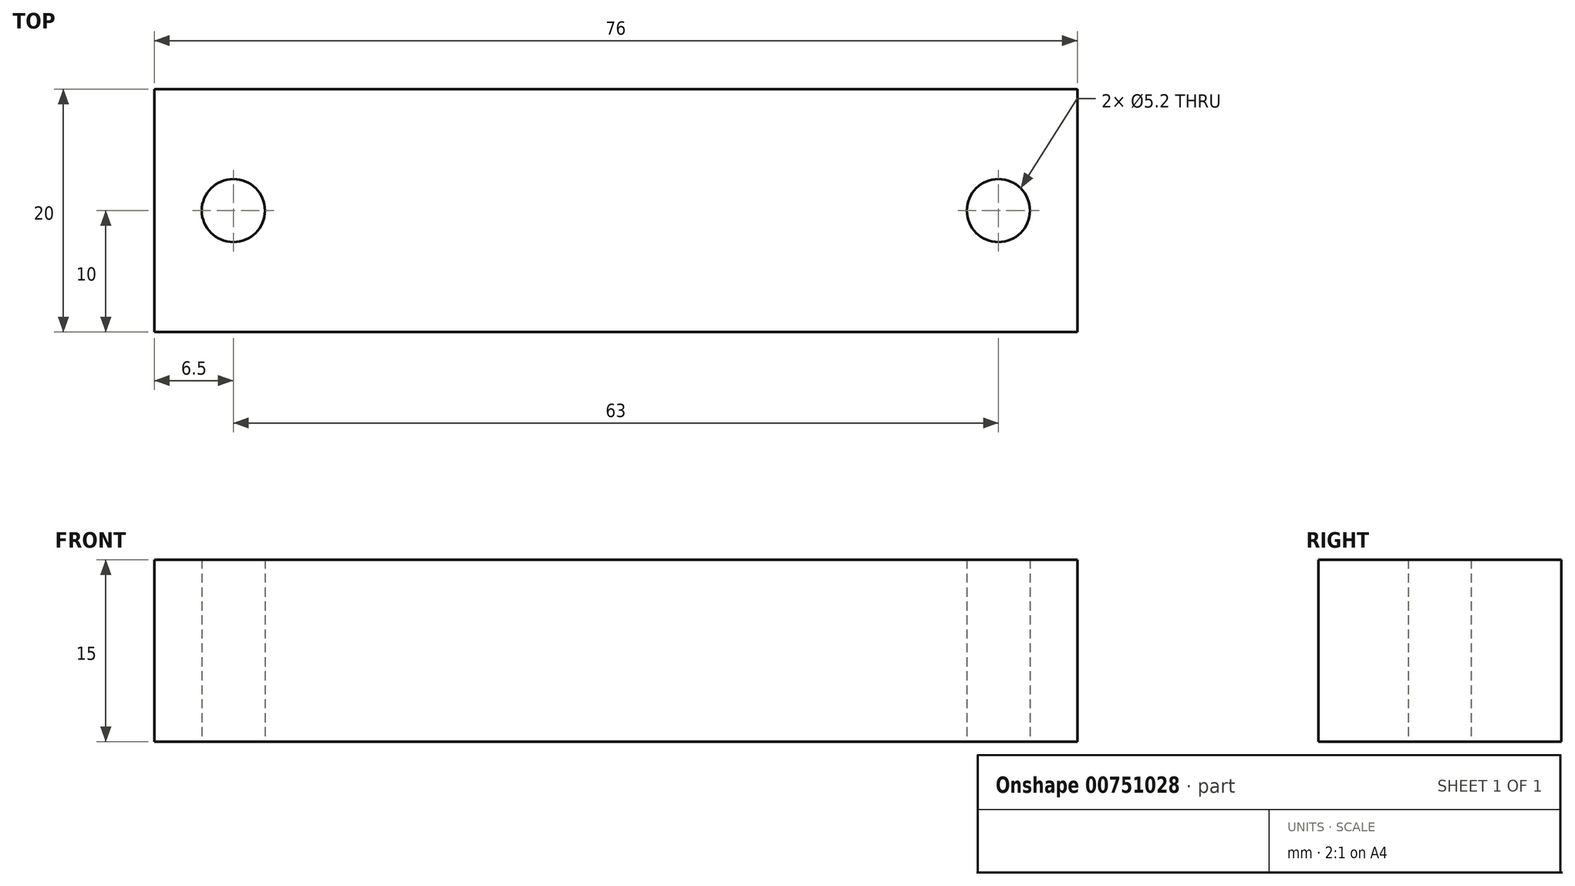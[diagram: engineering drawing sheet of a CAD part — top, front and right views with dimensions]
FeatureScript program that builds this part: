
annotation { "Feature Type Name" : "Feature", "Feature Type Description" : "" }
export const myFeature = defineFeature(function(context is Context, id is Id, definition is map)
    precondition{}
    {
        {
            var Q0;
            Q0=qCreatedBy(makeId("Top.planeOp"),FACE);
            var sketch = newSketch(context, id + "F0", { "sketchPlane" : qUnion([Q0])});
            skLineSegment(sketch, "E0.bottom", {"start": v(-38, -10) * mm, "end": v(38, -10) * mm});
            skLineSegment(sketch, "E0.top", {"start": v(-38, 10) * mm, "end": v(38, 10) * mm});
            skLineSegment(sketch, "E0.left", {"start": v(-38, -10) * mm, "end": v(-38, 10) * mm});
            skLineSegment(sketch, "E0.right", {"start": v(38, -10) * mm, "end": v(38, 10) * mm});
            skPoint(sketch, "E0.middle", {"position": v(0, 0) * mm});
            skCircle(sketch, "E1", {"center": v(-31.5, 0) * mm, "radius": 2.6 * mm});
            skCircle(sketch, "E2.MirrorC", {"center": v(31.5, 0) * mm, "radius": 2.6 * mm});
            skSolve(sketch);
        }
        {
            var Q0;
            Q0 = qSketchRegion(id + "F0", true);
            extrude(context, id + "F1", {"entities" : qUnion([Q0]), "depth" : 15 * mm, "offsetDistance" : 25 * mm});
        }
    });
